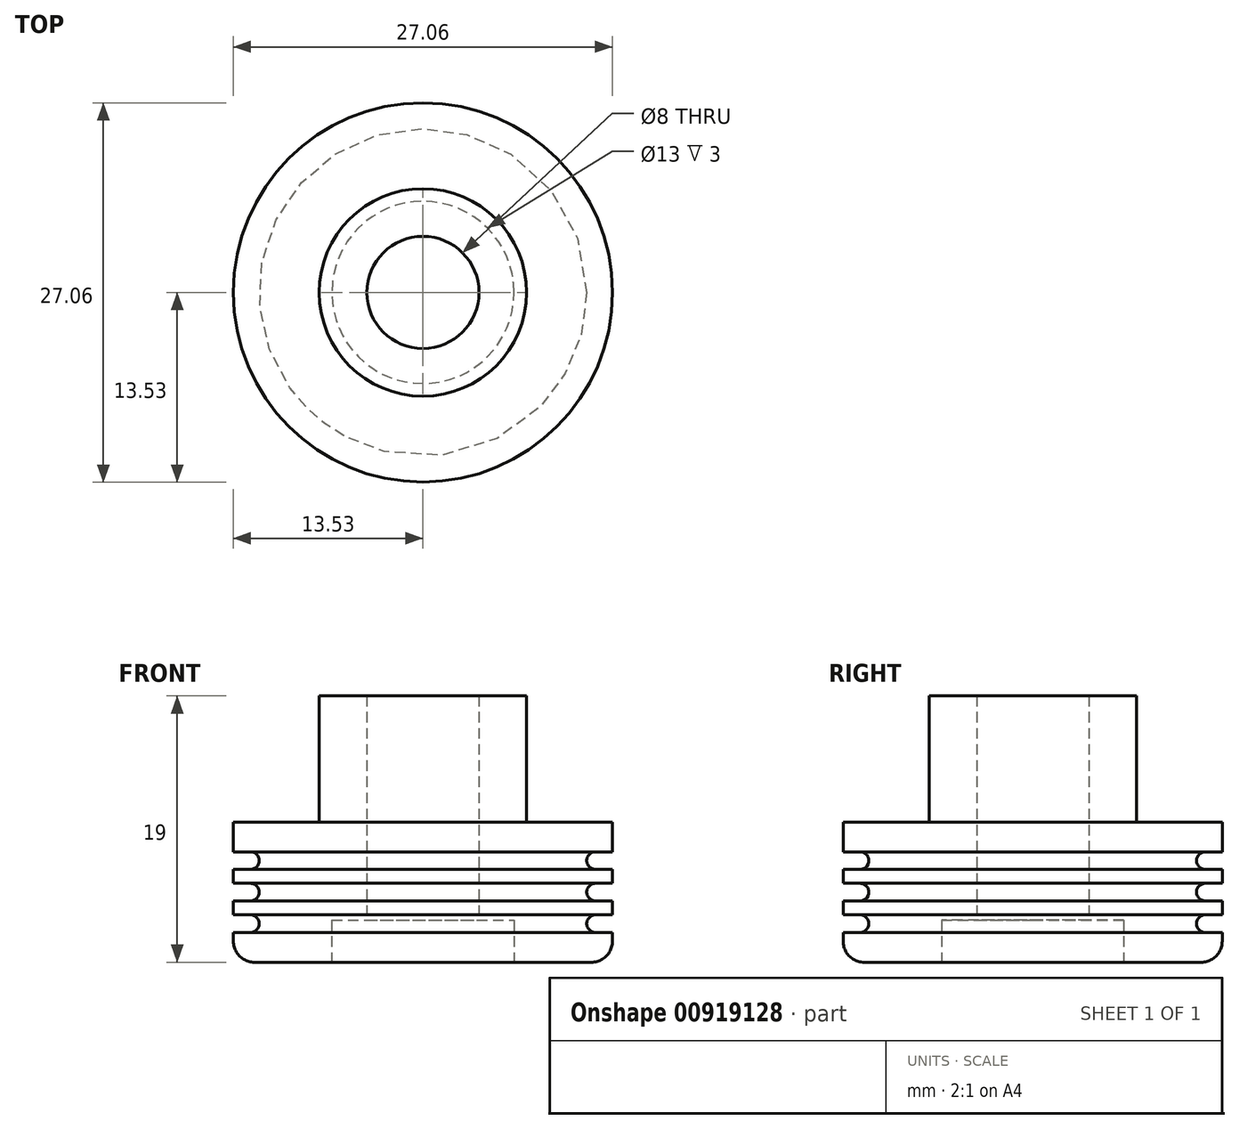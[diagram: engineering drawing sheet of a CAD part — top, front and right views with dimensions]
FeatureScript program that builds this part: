
annotation { "Feature Type Name" : "Feature", "Feature Type Description" : "" }
export const myFeature = defineFeature(function(context is Context, id is Id, definition is map)
    precondition{}
    {
        {
            var Q0;
            Q0=qCreatedBy(makeId("Top.planeOp"),FACE);
            var sketch = newSketch(context, id + "F0", { "sketchPlane" : qUnion([Q0])});
            skCircle(sketch, "E0", {"center": v(0, 0) * mm, "radius": 13.53 * mm});
            skCircle(sketch, "E1", {"center": v(0, 0) * mm, "radius": 4 * mm});
            skSolve(sketch);
        }
        {
            var Q0;
            Q0 = qSketchRegion(id + "F0", true);
            var Q1;
            Q1=makeQuery(id+"F0.imprint","IMPRINT",FACE,{"disambiguationData":[TD([[makeQuery(id+"F0.imprint","IMPRINT",EDGE,{"derivedFrom":sQuery(id+"F0.wireOp",EDGE,"iIRCAstM-g1SY-fqmb-iRLQ-sl72ryF1Clc2")}),1.0]])]});
            extrude(context, id + "F1", {"entities" : qUnion([Q0, Q1]), "depth" : 19 * mm, "offsetDistance" : 25 * mm});
        }
        {
            var Q0;
            Q0=makeQuery(id+"F1.opExtrude","CAP_FACE",FACE,{"disambiguationData":[OSD([sQuery(id+"F0.wireOp",EDGE,"E0"),sQuery(id+"F0.wireOp",EDGE,"E1")])],"isStart":true});
            var sketch = newSketch(context, id + "F2", { "sketchPlane" : qUnion([Q0])});
            skCircle(sketch, "E2", {"center": v(0, 0) * mm, "radius": 6.5 * mm});
            skSolve(sketch);
        }
        {
            var Q0;
            Q0 = qSketchRegion(id + "F2", true);
            extrude(context, id + "F3", {"entities" : qUnion([Q0]), "operationType" : NewBodyOperationType.REMOVE, "oppositeDirection" : true, "depth" : 3 * mm, "offsetDistance" : 25 * mm});
        }
        {
            var Q0;
            Q0=makeQuery(id+"F1.opExtrude","CAP_FACE",FACE,{"disambiguationData":[OSD([sQuery(id+"F0.wireOp",EDGE,"E0"),sQuery(id+"F0.wireOp",EDGE,"E1")])],"isStart":false});
            var sketch = newSketch(context, id + "F4", { "sketchPlane" : qUnion([Q0])});
            skCircle(sketch, "E3", {"center": v(0, 0) * mm, "radius": 7.4 * mm});
            skCircle(sketch, "E4", {"center": v(0, 0) * mm, "radius": 13.53 * mm});
            skSolve(sketch);
        }
        {
            var Q0;
            Q0 = qSketchRegion(id + "F4", true);
            extrude(context, id + "F5", {"entities" : qUnion([Q0]), "operationType" : NewBodyOperationType.REMOVE, "oppositeDirection" : true, "depth" : 9 * mm, "offsetDistance" : 25 * mm});
        }
        {
            var Q0;
            Q0=makeQuery(id+"F5.boolean.opBoolean","COPY",EDGE,{"derivedFrom":makeQuery(id+"F5.opExtrude","CAP_EDGE",EDGE,{"disambiguationData":[OSD([sQuery(id+"F4.wireOp",EDGE,"E4")])],"isStart":false})});
            var Q1;
            Q1=makeQuery(id+"F1.opExtrude","CAP_EDGE",EDGE,{"disambiguationData":[OSD([sQuery(id+"F0.wireOp",EDGE,"E0")])],"isStart":true});
            fillet(context, id + "F6", {"entities" : qUnion([Q0, Q1]), "radius" : 1.5 * mm, "tangentPropagation" : true, "allowEdgeOverflow" : false});
        }
        {
            var Q0;
            Q0=qCreatedBy(makeId("Right.planeOp"),FACE);
            var sketch = newSketch(context, id + "F7", { "sketchPlane" : qUnion([Q0])});
            skLineSegment(sketch, "E5", {"start": v(0, 0) * mm, "end": v(0, 20.43) * mm, "construction": true});
            skLineSegment(sketch, "E6", {"start": v(0, 0) * mm, "end": v(-14.32, 0) * mm});
            skLineSegment(sketch, "E7.bottom", {"start": v(-12.31, 3.38) * mm, "end": v(-17.31, 3.38) * mm});
            skLineSegment(sketch, "E7.top", {"start": v(-12.31, 2.12) * mm, "end": v(-17.31, 2.12) * mm});
            skLineSegment(sketch, "E7.right", {"start": v(-17.31, 3.38) * mm, "end": v(-17.31, 2.12) * mm});
            skPoint(sketch, "E7.middle", {"position": v(-14.81, 2.75) * mm});
            skLineSegment(sketch, "E8.bottom", {"start": v(-12.31, 5.62) * mm, "end": v(-17.31, 5.62) * mm});
            skLineSegment(sketch, "E8.top", {"start": v(-12.31, 4.37) * mm, "end": v(-17.31, 4.37) * mm});
            skLineSegment(sketch, "E8.right", {"start": v(-17.31, 5.62) * mm, "end": v(-17.31, 4.37) * mm});
            skPoint(sketch, "E8.middle", {"position": v(-14.81, 5) * mm});
            skLineSegment(sketch, "E9.bottom", {"start": v(-12.31, 7.88) * mm, "end": v(-17.31, 7.88) * mm});
            skLineSegment(sketch, "E9.top", {"start": v(-12.31, 6.63) * mm, "end": v(-17.31, 6.62) * mm});
            skLineSegment(sketch, "E9.right", {"start": v(-17.31, 7.88) * mm, "end": v(-17.31, 6.62) * mm});
            skPoint(sketch, "E9.middle", {"position": v(-14.81, 7.25) * mm});
            skLineSegment(sketch, "E10", {"start": v(-14.81, 0) * mm, "end": v(-14.81, 2.75) * mm});
            skPoint(sketch, "E10.startSnap0", {"position": v(-14.81, 2.12) * mm});
            skLineSegment(sketch, "E11", {"start": v(-14.81, 2.75) * mm, "end": v(-14.81, 5) * mm});
            skLineSegment(sketch, "E12", {"start": v(-14.81, 5) * mm, "end": v(-14.81, 7.25) * mm});
            skArc(sketch, "E13", {"start": v(-12.31, 2.12) * mm, "mid": v(-11.69, 2.75) * mm, "end": v(-12.31, 3.37) * mm});
            skArc(sketch, "E14", {"start": v(-12.31, 4.37) * mm, "mid": v(-11.69, 5) * mm, "end": v(-12.31, 5.62) * mm});
            skArc(sketch, "E15", {"start": v(-12.31, 6.62) * mm, "mid": v(-11.69, 7.25) * mm, "end": v(-12.31, 7.88) * mm});
            skSolve(sketch);
        }
        {
            var Q0;
            Q0 = qSketchRegion(id + "F7", true);
            var Q1;
            Q1=sQuery(id+"F7.wireOp",EDGE,"E5");
            revolve(context, id + "F8", {"operationType" : NewBodyOperationType.REMOVE, "surfaceOperationType" : NewSurfaceOperationType.NEW, "entities" : qUnion([Q0]), "axis" : qUnion([Q1]), "revolveType" : RevolveType.FULL, "oppositeDirection" : true});
        }
    });
